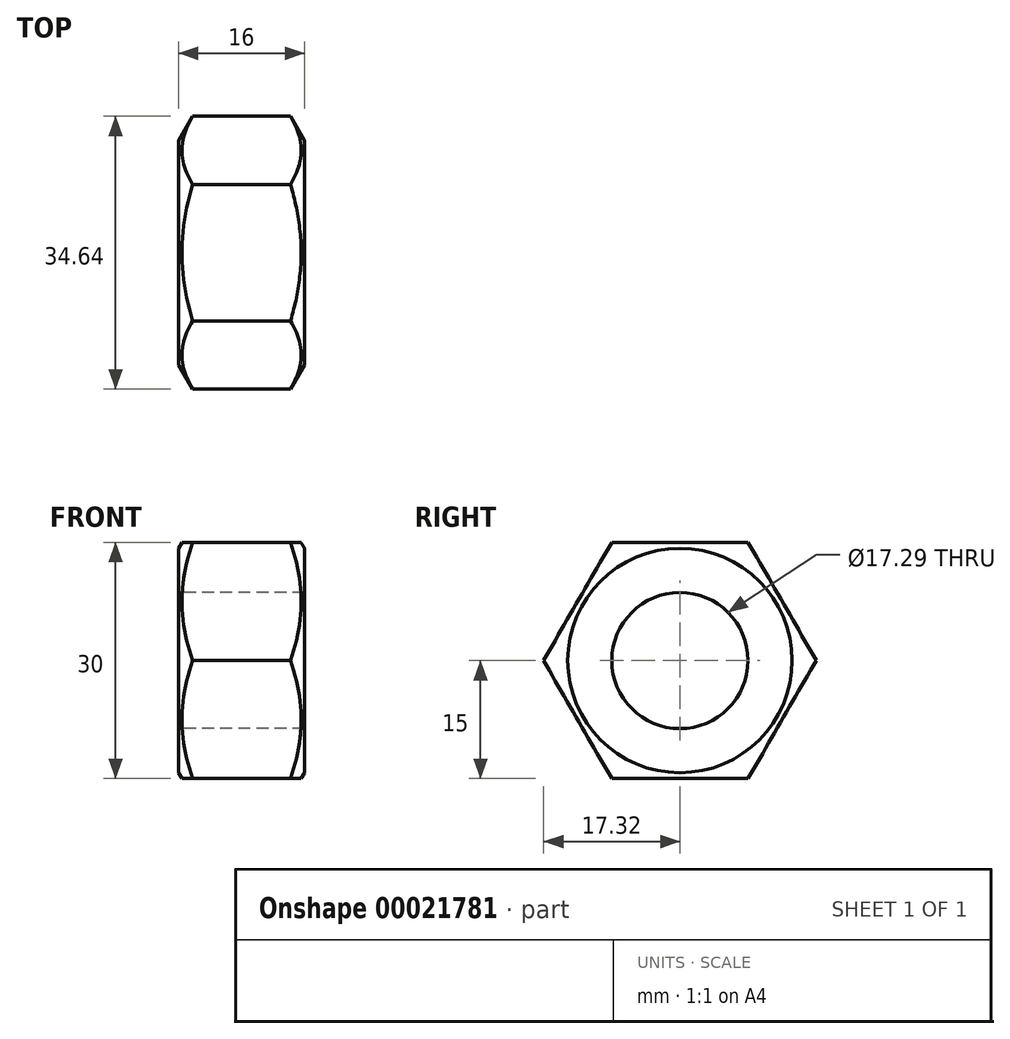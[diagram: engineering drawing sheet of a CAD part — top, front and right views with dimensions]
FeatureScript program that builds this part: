
annotation { "Feature Type Name" : "Feature", "Feature Type Description" : "" }
export const myFeature = defineFeature(function(context is Context, id is Id, definition is map)
    precondition{}
    {
        {
            var Q0;
            Q0=qCreatedBy(makeId("Front.planeOp"),FACE);
            var sketch = newSketch(context, id + "F1", { "sketchPlane" : qUnion([Q0])});
            skLineSegment(sketch, "E0", {"start": v(0, 8.65) * mm, "end": v(16, 8.65) * mm});
            skLineSegment(sketch, "E1", {"start": v(16, 8.65) * mm, "end": v(16, 14.25) * mm});
            skLineSegment(sketch, "E2", {"start": v(16, 14.25) * mm, "end": v(8, 28.1) * mm});
            skLineSegment(sketch, "E3", {"start": v(8, 28.1) * mm, "end": v(0, 14.25) * mm});
            skLineSegment(sketch, "E4", {"start": v(0, 14.25) * mm, "end": v(0, 8.65) * mm});
            skLineSegment(sketch, "E5", {"start": v(0, 0) * mm, "end": v(16, 0) * mm, "construction": true});
            skSolve(sketch);
        }
        {
            var Q0;
            Q0 = qSketchRegion(id + "F1", true);
            var Q1;
            Q1=sQuery(id+"F1.wireOp",EDGE,"E5");
            revolve(context, id + "F2", {"entities" : qUnion([Q0]), "axis" : qUnion([Q1]), "revolveType" : RevolveType.FULL});
        }
        {
            var Q0;
            Q0=makeQuery(id+"F2.opRevolve","SWEPT_FACE",FACE,{"disambiguationData":[OSD([sQuery(id+"F1.wireOp",EDGE,"E1")])]});
            var sketch = newSketch(context, id + "F3", { "sketchPlane" : qUnion([Q0])});
            skCircle(sketch, "E6.cCircle", {"center": v(0, 0) * mm, "radius": 15 * mm, "construction": true});
            skLineSegment(sketch, "E6.0", {"start": v(8.66, 15) * mm, "end": v(17.32, 0) * mm});
            skLineSegment(sketch, "E6.1", {"start": v(17.32, 0) * mm, "end": v(8.66, -15) * mm});
            skLineSegment(sketch, "E6.2", {"start": v(8.66, -15) * mm, "end": v(-8.66, -15) * mm});
            skLineSegment(sketch, "E6.3", {"start": v(-8.66, -15) * mm, "end": v(-17.32, 0) * mm});
            skLineSegment(sketch, "E6.4", {"start": v(-17.32, 0) * mm, "end": v(-8.66, 15) * mm});
            skLineSegment(sketch, "E6.5", {"start": v(-8.66, 15) * mm, "end": v(8.66, 15) * mm});
            skPoint(sketch, "E6.0.midPoint", {"position": v(13, 7.5) * mm});
            skCircle(sketch, "E7.0", {"center": v(0, 0) * mm, "radius": 28.1 * mm});
            skSolve(sketch);
        }
        {
            var Q0;
            Q0 = qSketchRegion(id + "F3", true);
            extrude(context, id + "F0", {"entities" : qUnion([Q0]), "operationType" : NewBodyOperationType.REMOVE, "endBound" : BoundingType.THROUGH_ALL, "oppositeDirection" : true, "depth" : 25 * mm});
        }
    });
